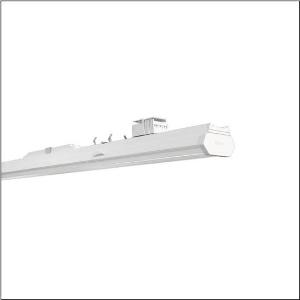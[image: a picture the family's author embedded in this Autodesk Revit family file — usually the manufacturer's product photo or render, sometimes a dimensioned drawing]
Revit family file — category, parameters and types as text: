
# Revit family: licross_r__11_protected_ho_51tp12mn4f5m_a747
name_source: partatom
category: Lighting Fixtures
units: mm (PartAtom-declared; Revit-internal decimal feet)

## family parameters
Cut with Voids When Loaded = No
Host = Face
Light Source = No
Part Type = Normal
Room Calculation Point = No
Round Connector Dimension = Use Diameter
Shared = No

## types (1)
- --- (1 x LED, 15820 lm, 87.4 W, 4000K)
    Apparent Load = 87 VA
    CIE Flux Codes = 70 91 97 98 100
    Color Rendering = 80
    Color Temperature = 4000K
    Default Elevation = 1800 mm
    Description = Licross® 11 Protected HO, luminaire insert, of sheet steel, galvanised, coil coated, white, length: 1.500mm, width: 90mm, height: 101mm, LED rated luminous flux: 15.820lm, light colour: 840, SDCM (Standard Deviation of Colour Matching)MacAdam ≤ 2 SDCM (initial), control gear: ON/OFF Multilumen, with plug, 3-pole, with phase selection, mains connection: 220..240V, AC, 50/60Hz, rated input power: 87W, internal wiring halogen-free, primary light control with lens, of plastic, primary optical cover: cover, of PMMA, light emission: direct distribution, primary light characteristic: symmetric, protection rating (complete): IP64, insulation class (complete): insulation class I (protective earthing), certification: CE, ENEC, VDE, UKCA, protection symbol: D if used in an environment with conductive dust loads with corresponding accessories, impact resistance: IK06, permissible ambient temperature for indoor applications: -35..+35°C, corresponds to IFS (International Featured Standards) requirements for safety and quality in the food industry, reducing of maximum allowable ambient temperature of 5°C with ceiling mounting, LABS conformity tested according to VDMA 24364:2018-05, packaging unit: 1 piece
    Height = 92 mm
    Lamp = 1 x LED
    Lamp Light Flux = 15820 lm
    Lamp Power = 87.4 W
    Lamp count = 1
    Length = 1500 mm
    Luminous efficacy = 181 lm/W
    Manufacturer = Siteco
    ModVariant = No
    Model = 51TP12MN4F5M
    Mounting Place = Ceiling
    Mounting Type = Pendant
    Number of Poles = 1
    OnlyDefault = Yes
    Power Factor = 1
    Product Name = Licross® 11 Protected HO
    Product group = luminaire insert | ceiling pendant
    ProductGroupID = 901
    Protection Class = Protection class I
    Protection Degree = IP 64
    RLX_Detail_Level = 1
    RLX_Emergency_Light_Flux = 0 lm
    RLX_Emergency_Type = 0
    RLX_Emergency_Type_DB = No
    RlxData = <blob elided: 22201 chars, md5=9df6c3a5>
    Socket = socket
    Standby Power = 0 W
    System Light Flux = 15820 lm
    System Power = 87 W
    Type Comments = factory setting: luminous flux: 100 % | (A | C | E) | 203 mA
    Type Image = l_1256148.jpg
    URL = http://relux.com
    VarID = @adj_093695
    Voltage = 0 V
    Weight = 0.00 kg
    Width = 88 mm

## geometry (parser evidence)
native form markers: Blend x4, Sweep x12
no freeform markers — native parametric forms only
